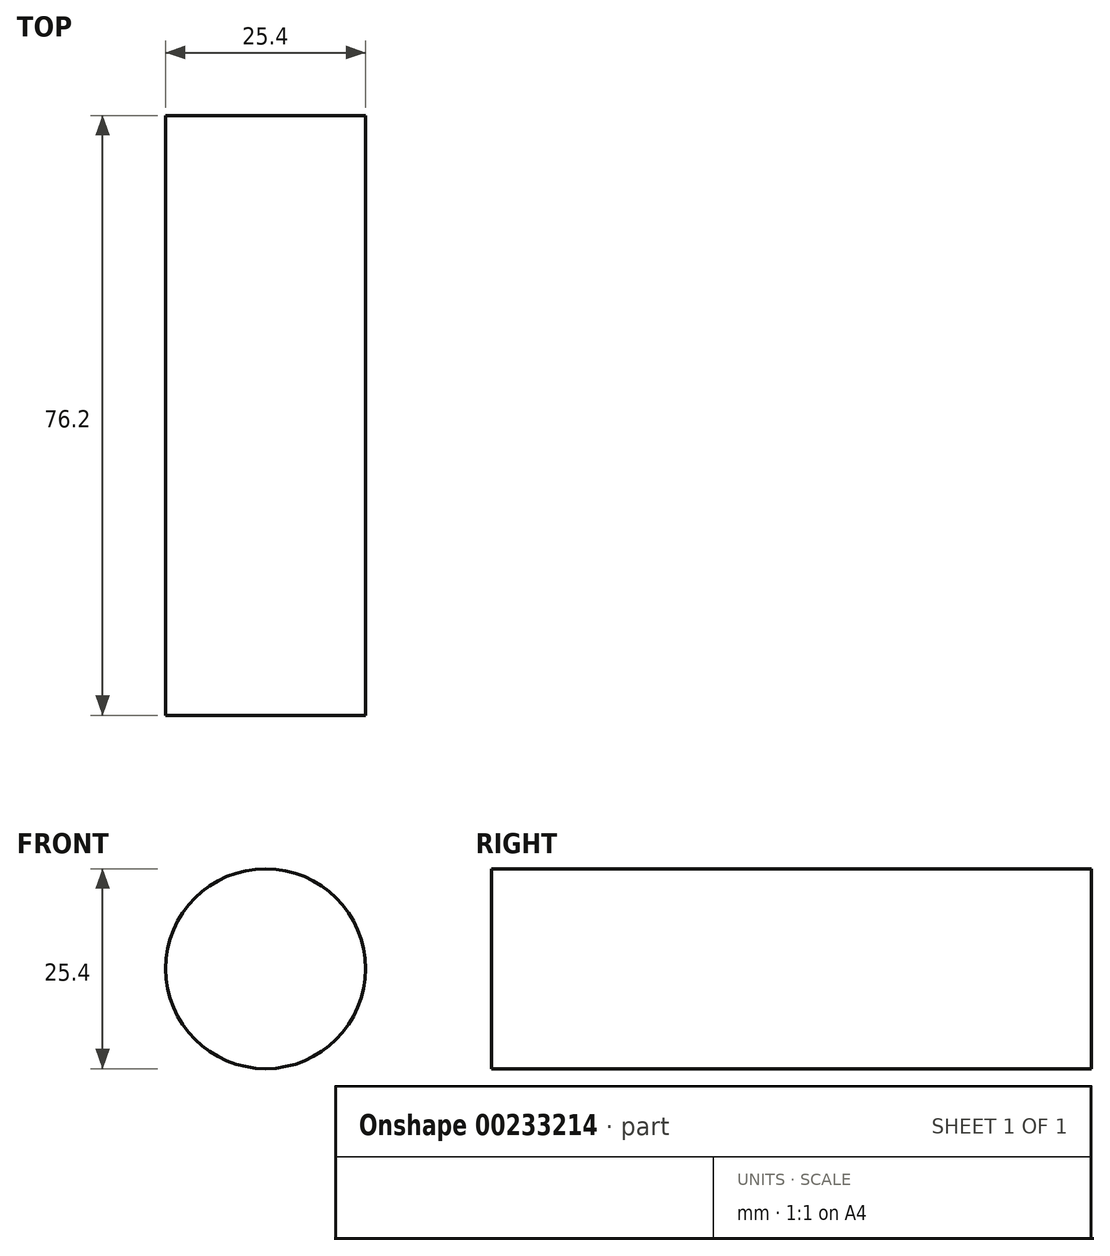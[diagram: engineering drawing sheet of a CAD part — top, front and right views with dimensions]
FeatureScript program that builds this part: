
annotation { "Feature Type Name" : "Feature", "Feature Type Description" : "" }
export const myFeature = defineFeature(function(context is Context, id is Id, definition is map)
    precondition{}
    {
        {
            var Q0;
            Q0=qCreatedBy(makeId("Front.planeOp"),FACE);
            var sketch = newSketch(context, id + "F0", { "sketchPlane" : qUnion([Q0])});
            skCircle(sketch, "E0", {"center": v(-28.09, 22.98) * mm, "radius": 12.7 * mm});
            skSolve(sketch);
        }
        {
            var Q0;
            Q0 = qSketchRegion(id + "F0", true);
            extrude(context, id + "F1", {"entities" : qUnion([Q0]), "depth" : 76.2 * mm});
        }
    });
